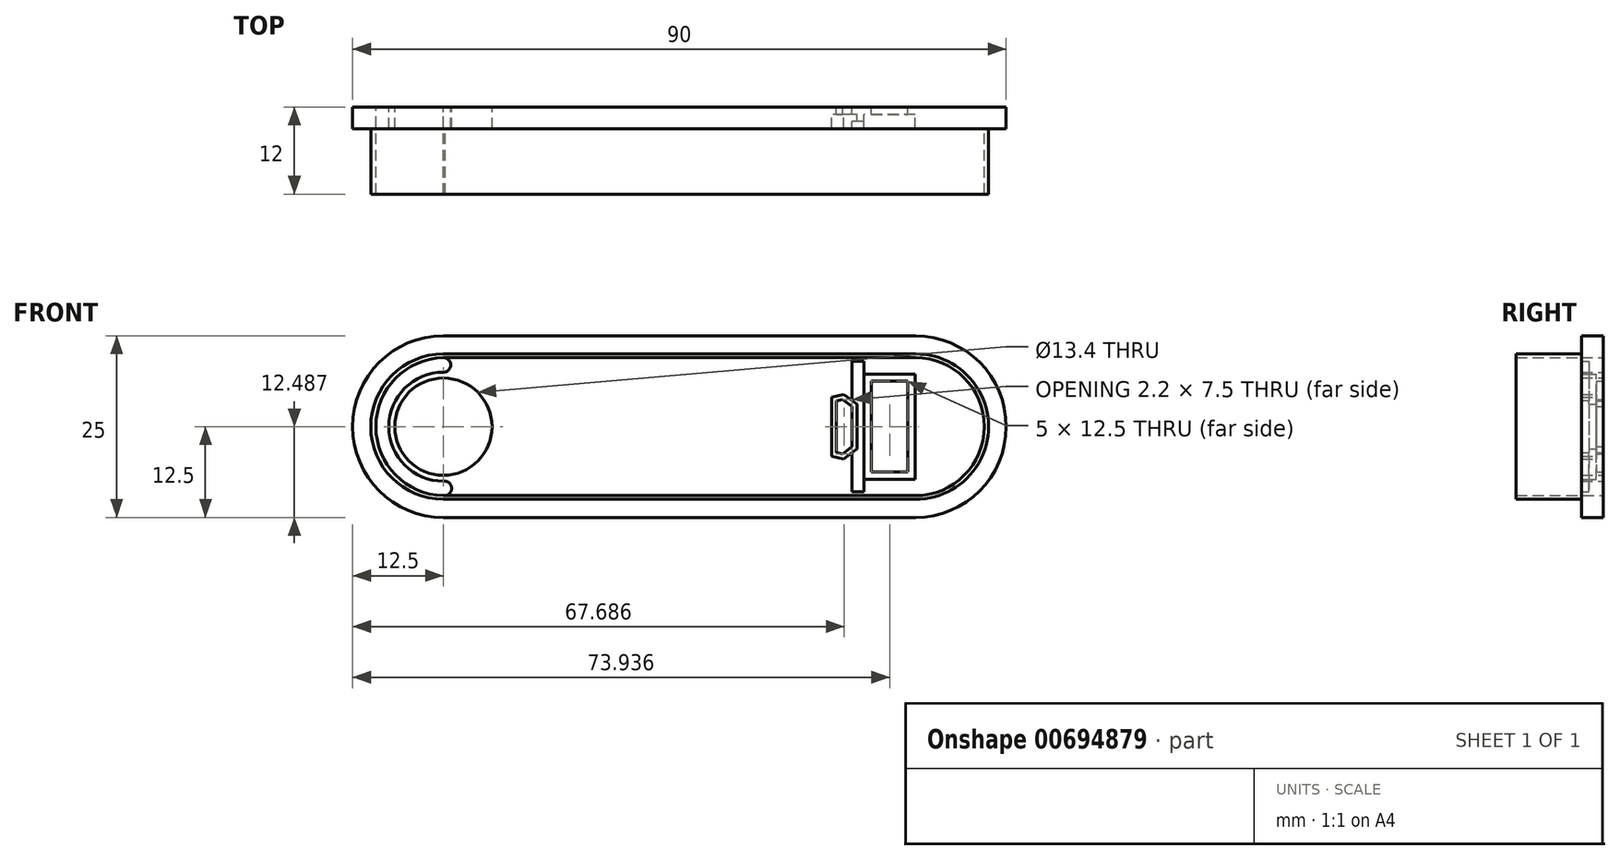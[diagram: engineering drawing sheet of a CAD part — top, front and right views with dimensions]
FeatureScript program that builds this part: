
annotation { "Feature Type Name" : "Feature", "Feature Type Description" : "" }
export const myFeature = defineFeature(function(context is Context, id is Id, definition is map)
    precondition{}
    {
        {
            var Q0;
            Q0=qCreatedBy(makeId("Front.planeOp"),FACE);
            var sketch = newSketch(context, id + "F0", { "sketchPlane" : qUnion([Q0])});
            skLineSegment(sketch, "E0.bottom", {"start": v(0, 0) * mm, "end": v(-65, 0) * mm});
            skLineSegment(sketch, "E0.top", {"start": v(0, 25) * mm, "end": v(-65, 25) * mm});
            skArc(sketch, "E1", {"start": v(-65, 25) * mm, "mid": v(-77.5, 12.5) * mm, "end": v(-65, 0) * mm});
            skArc(sketch, "E2", {"start": v(0, 0) * mm, "mid": v(12.5, 12.5) * mm, "end": v(0, 25) * mm});
            skArc(sketch, "E3", {"start": v(-65, 19.99) * mm, "mid": v(-72.5, 12.49) * mm, "end": v(-65, 4.99) * mm});
            skArc(sketch, "E4", {"start": v(-65, 22) * mm, "mid": v(-74.29, 12.5) * mm, "end": v(-65, 3) * mm});
            skArc(sketch, "E5", {"start": v(-65, 19.99) * mm, "mid": v(-64, 21) * mm, "end": v(-65, 22) * mm});
            skArc(sketch, "E6", {"start": v(-65, 3) * mm, "mid": v(-63.87, 4) * mm, "end": v(-65, 4.99) * mm});
            skArc(sketch, "E7", {"start": v(-65, 22) * mm, "mid": v(-74.3, 12.5) * mm, "end": v(-65, 3) * mm});
            skCircle(sketch, "E8", {"center": v(-65, 12.49) * mm, "radius": 6.7 * mm});
            skArc(sketch, "E9", {"start": v(0, 3) * mm, "mid": v(9.5, 12.5) * mm, "end": v(0, 22) * mm});
            skArc(sketch, "E10", {"start": v(-65, 22.5) * mm, "mid": v(-75, 12.5) * mm, "end": v(-65, 2.5) * mm});
            skArc(sketch, "E11", {"start": v(0, 2.5) * mm, "mid": v(10.06, 12.5) * mm, "end": v(0, 22.5) * mm});
            skLineSegment(sketch, "E12", {"start": v(-65, 22.5) * mm, "end": v(0, 22.5) * mm});
            skLineSegment(sketch, "E13", {"start": v(0, 2.5) * mm, "end": v(-65, 2.5) * mm});
            skLineSegment(sketch, "E14", {"start": v(-65, 3) * mm, "end": v(0, 3) * mm});
            skLineSegment(sketch, "E15", {"start": v(-65, 22) * mm, "end": v(0, 22) * mm});
            skLineSegment(sketch, "E16", {"start": v(-0.06, 19.75) * mm, "end": v(-0.06, 5.25) * mm});
            skLineSegment(sketch, "E17", {"start": v(-0.06, 19.75) * mm, "end": v(-7.06, 19.75) * mm});
            skLineSegment(sketch, "E18", {"start": v(-7.06, 19.75) * mm, "end": v(-0.06, 19.75) * mm});
            skLineSegment(sketch, "E19", {"start": v(-0.06, 5.25) * mm, "end": v(-7.06, 5.25) * mm});
            skLineSegment(sketch, "E20", {"start": v(-7.06, 5.25) * mm, "end": v(-7.06, 19.75) * mm});
            skLineSegment(sketch, "E21", {"start": v(-7.06, 19.75) * mm, "end": v(-7.06, 21.5) * mm});
            skArc(sketch, "E22.MirrorCS", {"start": v(-65, 3) * mm, "mid": v(-74.3, 12.5) * mm, "end": v(-65, 22) * mm});
            skArc(sketch, "E23.MirrorCS", {"start": v(-65, 2.5) * mm, "mid": v(-75, 12.5) * mm, "end": v(-65, 22.5) * mm});
            skLineSegment(sketch, "E24.MirrorCS", {"start": v(-7.06, 5.25) * mm, "end": v(-7.06, 3.5) * mm});
            skLineSegment(sketch, "E25", {"start": v(-7.06, 3.5) * mm, "end": v(-8.71, 3.5) * mm});
            skLineSegment(sketch, "E26", {"start": v(-8.71, 3.5) * mm, "end": v(-8.71, 8.93) * mm});
            skLineSegment(sketch, "E27", {"start": v(0, 3) * mm, "end": v(0, 2.5) * mm});
            skLineSegment(sketch, "E28.MirrorCS", {"start": v(-7.06, 21.5) * mm, "end": v(-8.71, 21.5) * mm});
            skLineSegment(sketch, "E29", {"start": v(-7.06, 3.5) * mm, "end": v(-7.06, 9.43) * mm});
            skLineSegment(sketch, "E30.MirrorCS", {"start": v(-8.71, 21.5) * mm, "end": v(-8.71, 16.07) * mm});
            skLineSegment(sketch, "E31", {"start": v(-7.06, 3.5) * mm, "end": v(-7.06, 12.5) * mm});
            skLineSegment(sketch, "E32", {"start": v(-6.06, 18.75) * mm, "end": v(-1.06, 18.75) * mm});
            skLineSegment(sketch, "E33", {"start": v(-1.06, 6.25) * mm, "end": v(-1.06, 18.75) * mm});
            skLineSegment(sketch, "E34", {"start": v(-6.06, 18.75) * mm, "end": v(-6.06, 6.25) * mm});
            skLineSegment(sketch, "E35", {"start": v(-6.06, 6.25) * mm, "end": v(-1.06, 6.25) * mm});
            skLineSegment(sketch, "E36", {"start": v(-8.06, 9.43) * mm, "end": v(-8.71, 8.93) * mm});
            skLineSegment(sketch, "E37", {"start": v(-8.06, 9.43) * mm, "end": v(-9.86, 8.05) * mm});
            skLineSegment(sketch, "E38.MirrorCS", {"start": v(-8.06, 15.57) * mm, "end": v(-9.86, 16.95) * mm});
            skLineSegment(sketch, "E39", {"start": v(-8.06, 15.57) * mm, "end": v(-8.06, 9.43) * mm});
            skLineSegment(sketch, "E40", {"start": v(-8.71, 15.25) * mm, "end": v(-8.71, 9.75) * mm});
            skLineSegment(sketch, "E41", {"start": v(-8.71, 15.25) * mm, "end": v(-10.01, 16.25) * mm});
            skLineSegment(sketch, "E42.MirrorCS", {"start": v(-8.71, 9.75) * mm, "end": v(-10.01, 8.75) * mm});
            skLineSegment(sketch, "E43", {"start": v(-8.71, 9.75) * mm, "end": v(-10.91, 9.75) * mm});
            skLineSegment(sketch, "E44", {"start": v(-10.91, 8.95) * mm, "end": v(-10.01, 8.75) * mm});
            skLineSegment(sketch, "E45.MirrorCS", {"start": v(-10.91, 16.05) * mm, "end": v(-10.01, 16.25) * mm});
            skLineSegment(sketch, "E46", {"start": v(-10.91, 8.95) * mm, "end": v(-10.91, 16.05) * mm});
            skLineSegment(sketch, "E47", {"start": v(-11.56, 16.57) * mm, "end": v(-11.56, 12.5) * mm});
            skLineSegment(sketch, "E48", {"start": v(-9.86, 16.95) * mm, "end": v(-11.56, 16.57) * mm});
            skLineSegment(sketch, "E49.MirrorCS", {"start": v(-9.86, 8.05) * mm, "end": v(-11.56, 8.43) * mm});
            skLineSegment(sketch, "E50.MirrorCS", {"start": v(-11.56, 8.43) * mm, "end": v(-11.56, 12.5) * mm});
            skSolve(sketch);
        }
        {
            var Q0;
            {var subQ13=sQuery(id+"F0.wireOp",EDGE,"E5");Q0=makeQuery(id+"F0.imprint","IMPRINT",FACE,{"disambiguationData":[TD([[makeQuery(id+"F0.imprint","IMPRINT",EDGE,{"derivedFrom":subQ13}),-1.0]])]});}
            var Q1;
            {var subQ7=sQuery(id+"F0.wireOp",EDGE,"dbuLjMLx-MOiP-RQnc-3us2-xXklv9JgFWH2");Q1=makeQuery(id+"F0.imprint","IMPRINT",FACE,{"disambiguationData":[TD([[makeQuery(id+"F0.imprint","IMPRINT",EDGE,{"derivedFrom":subQ7}),-1.0]])]});}
            var Q2;
            {var subQ13=sQuery(id+"F0.wireOp",EDGE,"E19");Q2=makeQuery(id+"F0.imprint","IMPRINT",FACE,{"disambiguationData":[TD([[makeQuery(id+"F0.imprint","IMPRINT",EDGE,{"derivedFrom":subQ13}),1.0]])]});}
            var Q3;
            {var subQ0=sQuery(id+"F0.wireOp",EDGE,"86e7032f-2ca0-463b-bfbc-0645e4a0909b.0");var subQ1=sQuery(id+"F0.wireOp",EDGE,"E3");var subQ2=makeQuery(id+"F0.imprint","INTERSECT",VERTEX,{"derivedFrom":[subQ1,subQ0]});Q3=makeQuery(id+"F0.imprint","IMPRINT",FACE,{"disambiguationData":[TD([[makeQuery(id+"F0.imprint","IMPRINT",EDGE,{"disambiguationData":[TD([[subQ2,-1.0]])],"derivedFrom":subQ1}),1.0]])]});}
            var Q4;
            {var subQ5=sQuery(id+"F0.wireOp",EDGE,"E0.top");Q4=makeQuery(id+"F0.imprint","IMPRINT",FACE,{"disambiguationData":[TD([[makeQuery(id+"F0.imprint","IMPRINT",EDGE,{"derivedFrom":subQ5}),1.0]])]});}
            var Q5;
            {var subQ0=sQuery(id+"F0.wireOp",EDGE,"86e7032f-2ca0-463b-bfbc-0645e4a0909b.0");var subQ1=sQuery(id+"F0.wireOp",EDGE,"E1");var subQ2=makeQuery(id+"F0.imprint","INTERSECT",VERTEX,{"derivedFrom":[subQ1,subQ0]});Q5=makeQuery(id+"F0.imprint","IMPRINT",FACE,{"disambiguationData":[TD([[makeQuery(id+"F0.imprint","IMPRINT",EDGE,{"disambiguationData":[TD([[subQ2,-1.0]])],"derivedFrom":subQ1}),1.0]])]});}
            var Q6;
            {var subQ5=sQuery(id+"F0.wireOp",EDGE,"E0.bottom");Q6=makeQuery(id+"F0.imprint","IMPRINT",FACE,{"disambiguationData":[TD([[makeQuery(id+"F0.imprint","IMPRINT",EDGE,{"derivedFrom":subQ5}),-1.0]])]});}
            var Q7;
            {var subQ0=sQuery(id+"F0.wireOp",EDGE,"Dcb5nuMu-WByH-uQz3-wIFP-wi0rErrBsMwV");var subQ1=sQuery(id+"F0.wireOp",EDGE,"E2");var subQ2=makeQuery(id+"F0.imprint","INTERSECT",VERTEX,{"derivedFrom":[subQ1,subQ0]});Q7=makeQuery(id+"F0.imprint","IMPRINT",FACE,{"disambiguationData":[TD([[makeQuery(id+"F0.imprint","IMPRINT",EDGE,{"disambiguationData":[TD([[subQ2,-1.0]])],"derivedFrom":subQ1}),1.0]])]});}
            var Q8;
            {var subQ5=sQuery(id+"F0.wireOp",EDGE,"Dcb5nuMu-WByH-uQz3-wIFP-wi0rErrBsMwV");var subQ6=makeQuery(id+"F0.imprint","IMPRINT",VERTEX,{"disambiguationData":[OD(0.0)],"derivedFrom":subQ5});Q8=makeQuery(id+"F0.imprint","IMPRINT",FACE,{"disambiguationData":[TD([[makeQuery(id+"F0.imprint","IMPRINT",EDGE,{"disambiguationData":[TD([[subQ6,1.0]])],"derivedFrom":subQ5}),-1.0]])]});}
            extrude(context, id + "F1", {"entities" : qUnion([Q0, Q1, Q2, Q3, Q4, Q5, Q6, Q7, Q8]), "depth" : 3 * mm, "offsetDistance" : 25 * mm});
        }
        {
            var Q0;
            {var subQ9=sQuery(id+"F0.wireOp",EDGE,"dbuLjMLx-MOiP-RQnc-3us2-xXklv9JgFWH2");Q0=makeQuery(id+"F0.imprint","IMPRINT",FACE,{"disambiguationData":[TD([[makeQuery(id+"F0.imprint","IMPRINT",EDGE,{"derivedFrom":subQ9}),1.0]])]});}
            var Q1;
            {var subQ6=sQuery(id+"F0.wireOp",EDGE,"E28.MirrorCS");Q1=makeQuery(id+"F0.imprint","IMPRINT",FACE,{"disambiguationData":[TD([[makeQuery(id+"F0.imprint","IMPRINT",EDGE,{"derivedFrom":subQ6}),1.0]])]});}
            var Q2;
            {var subQ3=sQuery(id+"F0.wireOp",EDGE,"E25");Q2=makeQuery(id+"F0.imprint","IMPRINT",FACE,{"disambiguationData":[TD([[makeQuery(id+"F0.imprint","IMPRINT",EDGE,{"derivedFrom":subQ3}),-1.0]])]});}
            extrude(context, id + "F2", {"entities" : qUnion([Q0, Q1, Q2]), "operationType" : NewBodyOperationType.ADD, "depth" : 2 * mm, "offsetDistance" : 25 * mm});
        }
        {
            var Q0;
            {var subQ5=sQuery(id+"F0.wireOp",EDGE,"E18");Q0=makeQuery(id+"F0.imprint","IMPRINT",FACE,{"disambiguationData":[TD([[makeQuery(id+"F0.imprint","IMPRINT",EDGE,{"derivedFrom":subQ5}),-1.0]])]});}
            var Q1;
            {var subQ1=sQuery(id+"F0.wireOp",EDGE,"E20");var subQ3=sQuery(id+"F0.wireOp",EDGE,"86e7032f-2ca0-463b-bfbc-0645e4a0909b.0");var subQ4=makeQuery(id+"F0.imprint","INTERSECT",VERTEX,{"derivedFrom":[subQ1,subQ3]});Q1=makeQuery(id+"F0.imprint","IMPRINT",FACE,{"disambiguationData":[TD([[makeQuery(id+"F0.imprint","IMPRINT",EDGE,{"disambiguationData":[TD([[subQ4,1.0]])],"derivedFrom":subQ3}),1.0]])]});}
            var Q2;
            {var subQ11=sQuery(id+"F0.wireOp",EDGE,"E19");Q2=makeQuery(id+"F0.imprint","IMPRINT",FACE,{"disambiguationData":[TD([[makeQuery(id+"F0.imprint","IMPRINT",EDGE,{"derivedFrom":subQ11}),-1.0]])]});}
            var Q3;
            {var subQ0=sQuery(id+"F0.wireOp",EDGE,"E16");var subQ1=sQuery(id+"F0.wireOp",EDGE,"Dcb5nuMu-WByH-uQz3-wIFP-wi0rErrBsMwV");var subQ2=makeQuery(id+"F0.imprint","INTERSECT",VERTEX,{"derivedFrom":[subQ1,subQ0]});Q3=makeQuery(id+"F0.imprint","IMPRINT",FACE,{"disambiguationData":[TD([[makeQuery(id+"F0.imprint","IMPRINT",EDGE,{"disambiguationData":[TD([[subQ2,-1.0]])],"derivedFrom":subQ1}),-1.0]])]});}
            var Q4;
            {var subQ1=sQuery(id+"F0.wireOp",EDGE,"E39");Q4=makeQuery(id+"F0.imprint","IMPRINT",FACE,{"disambiguationData":[TD([[makeQuery(id+"F0.imprint","IMPRINT",EDGE,{"derivedFrom":subQ1}),-1.0]])]});}
            extrude(context, id + "F3", {"entities" : qUnion([Q0, Q1, Q2, Q3, Q4]), "operationType" : NewBodyOperationType.ADD, "depth" : 1 * mm, "offsetDistance" : 25 * mm});
        }
        {
            var Q0;
            {var subQ0=sQuery(id+"F0.wireOp",EDGE,"E12");Q0=makeQuery(id+"F0.imprint","IMPRINT",FACE,{"disambiguationData":[TD([[makeQuery(id+"F0.imprint","IMPRINT",EDGE,{"derivedFrom":subQ0}),-1.0]])]});}
            var Q1;
            {var subQ0=sQuery(id+"F0.wireOp",EDGE,"Dcb5nuMu-WByH-uQz3-wIFP-wi0rErrBsMwV");var subQ1=sQuery(id+"F0.wireOp",EDGE,"E9");var subQ2=makeQuery(id+"F0.imprint","INTERSECT",VERTEX,{"derivedFrom":[subQ1,subQ0]});Q1=makeQuery(id+"F0.imprint","IMPRINT",FACE,{"disambiguationData":[TD([[makeQuery(id+"F0.imprint","IMPRINT",EDGE,{"disambiguationData":[TD([[subQ2,-1.0]])],"derivedFrom":subQ1}),-1.0]])]});}
            var Q2;
            {var subQ0=sQuery(id+"F0.wireOp",EDGE,"E27");Q2=makeQuery(id+"F0.imprint","IMPRINT",FACE,{"disambiguationData":[TD([[makeQuery(id+"F0.imprint","IMPRINT",EDGE,{"derivedFrom":subQ0}),1.0]])]});}
            var Q3;
            {var subQ4=sQuery(id+"F0.wireOp",EDGE,"E13");Q3=makeQuery(id+"F0.imprint","IMPRINT",FACE,{"disambiguationData":[TD([[makeQuery(id+"F0.imprint","IMPRINT",EDGE,{"derivedFrom":subQ4}),-1.0]])]});}
            var Q4;
            {var subQ3=sQuery(id+"F0.wireOp",EDGE,"Dcb5nuMu-WByH-uQz3-wIFP-wi0rErrBsMwV");var subQ5=sQuery(id+"F0.wireOp",EDGE,"E23.MirrorCS");var subQ6=makeQuery(id+"F0.imprint","INTERSECT",VERTEX,{"derivedFrom":[subQ3,subQ5]});Q4=makeQuery(id+"F0.imprint","IMPRINT",FACE,{"disambiguationData":[TD([[makeQuery(id+"F0.imprint","IMPRINT",EDGE,{"disambiguationData":[TD([[subQ6,-1.0]])],"derivedFrom":subQ5}),-1.0]])]});}
            extrude(context, id + "F4", {"entities" : qUnion([Q0, Q1, Q2, Q3, Q4]), "operationType" : NewBodyOperationType.ADD, "depth" : 12 * mm, "offsetDistance" : 25 * mm});
        }
    });
